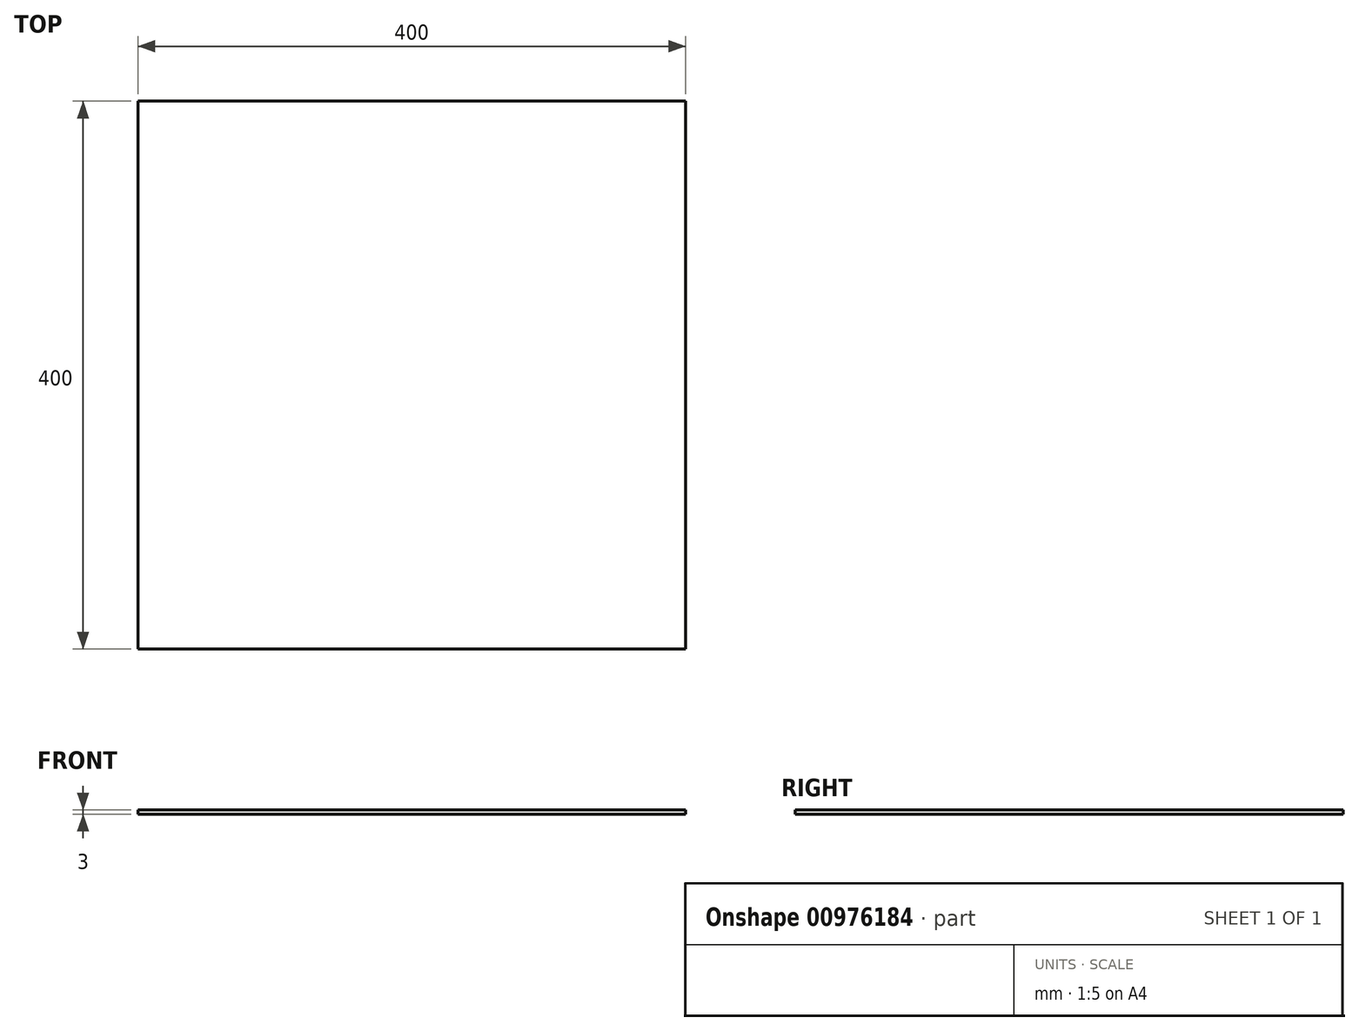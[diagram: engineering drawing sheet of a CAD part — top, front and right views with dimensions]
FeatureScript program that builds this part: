
annotation { "Feature Type Name" : "Feature", "Feature Type Description" : "" }
export const myFeature = defineFeature(function(context is Context, id is Id, definition is map)
    precondition{}
    {
        {
            var Q0;
            Q0=qCreatedBy(makeId("Top.planeOp"),FACE);
            var sketch = newSketch(context, id + "F0", { "sketchPlane" : qUnion([Q0])});
            skLineSegment(sketch, "E0.bottom", {"start": v(200, 200) * mm, "end": v(-200, 200) * mm});
            skLineSegment(sketch, "E0.top", {"start": v(200, -200) * mm, "end": v(-200, -200) * mm});
            skLineSegment(sketch, "E0.left", {"start": v(200, 200) * mm, "end": v(200, -200) * mm});
            skLineSegment(sketch, "E0.right", {"start": v(-200, 200) * mm, "end": v(-200, -200) * mm});
            skPoint(sketch, "E0.middle", {"position": v(0, 0) * mm});
            skSolve(sketch);
        }
        {
            var Q0;
            Q0 = qSketchRegion(id + "F0", true);
            extrude(context, id + "F1", {"entities" : qUnion([Q0]), "depth" : 3 * mm, "offsetDistance" : 25 * mm});
        }
    });
